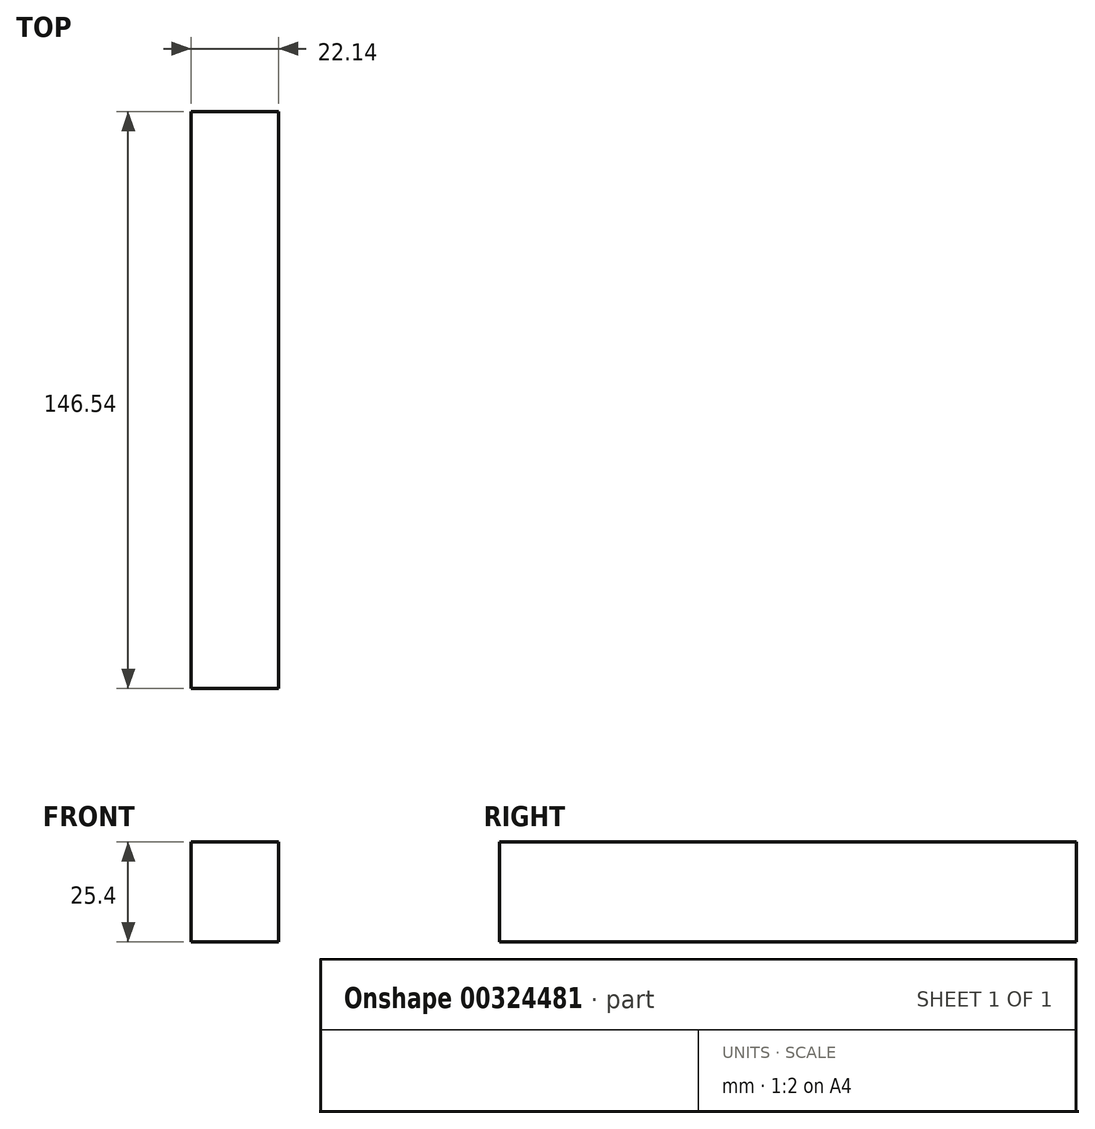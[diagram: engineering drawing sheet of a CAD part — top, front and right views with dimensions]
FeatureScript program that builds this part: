
annotation { "Feature Type Name" : "Feature", "Feature Type Description" : "" }
export const myFeature = defineFeature(function(context is Context, id is Id, definition is map)
    precondition{}
    {
        {
            var Q0;
            Q0=qCreatedBy(makeId("Top.planeOp"),FACE);
            var sketch = newSketch(context, id + "F0", { "sketchPlane" : qUnion([Q0])});
            skLineSegment(sketch, "E0.bottom", {"start": v(-75.8, 76.4) * mm, "end": v(-53.66, 76.4) * mm});
            skLineSegment(sketch, "E0.top", {"start": v(-75.8, -70.14) * mm, "end": v(-53.66, -70.14) * mm});
            skLineSegment(sketch, "E0.left", {"start": v(-75.8, 76.4) * mm, "end": v(-75.8, -70.14) * mm});
            skLineSegment(sketch, "E0.right", {"start": v(-53.66, 76.4) * mm, "end": v(-53.66, -70.14) * mm});
            skSolve(sketch);
        }
        {
            var Q0;
            Q0=makeQuery(id+"F0.imprint","IMPRINT",FACE,{"disambiguationData":[TD([[makeQuery(id+"F0.imprint","IMPRINT",EDGE,{"derivedFrom":sQuery(id+"F0.wireOp",EDGE,"E0.bottom")}),-1.0]])]});
            extrude(context, id + "F1", {"entities" : qUnion([Q0]), "depth" : 25.4 * mm});
        }
    });
